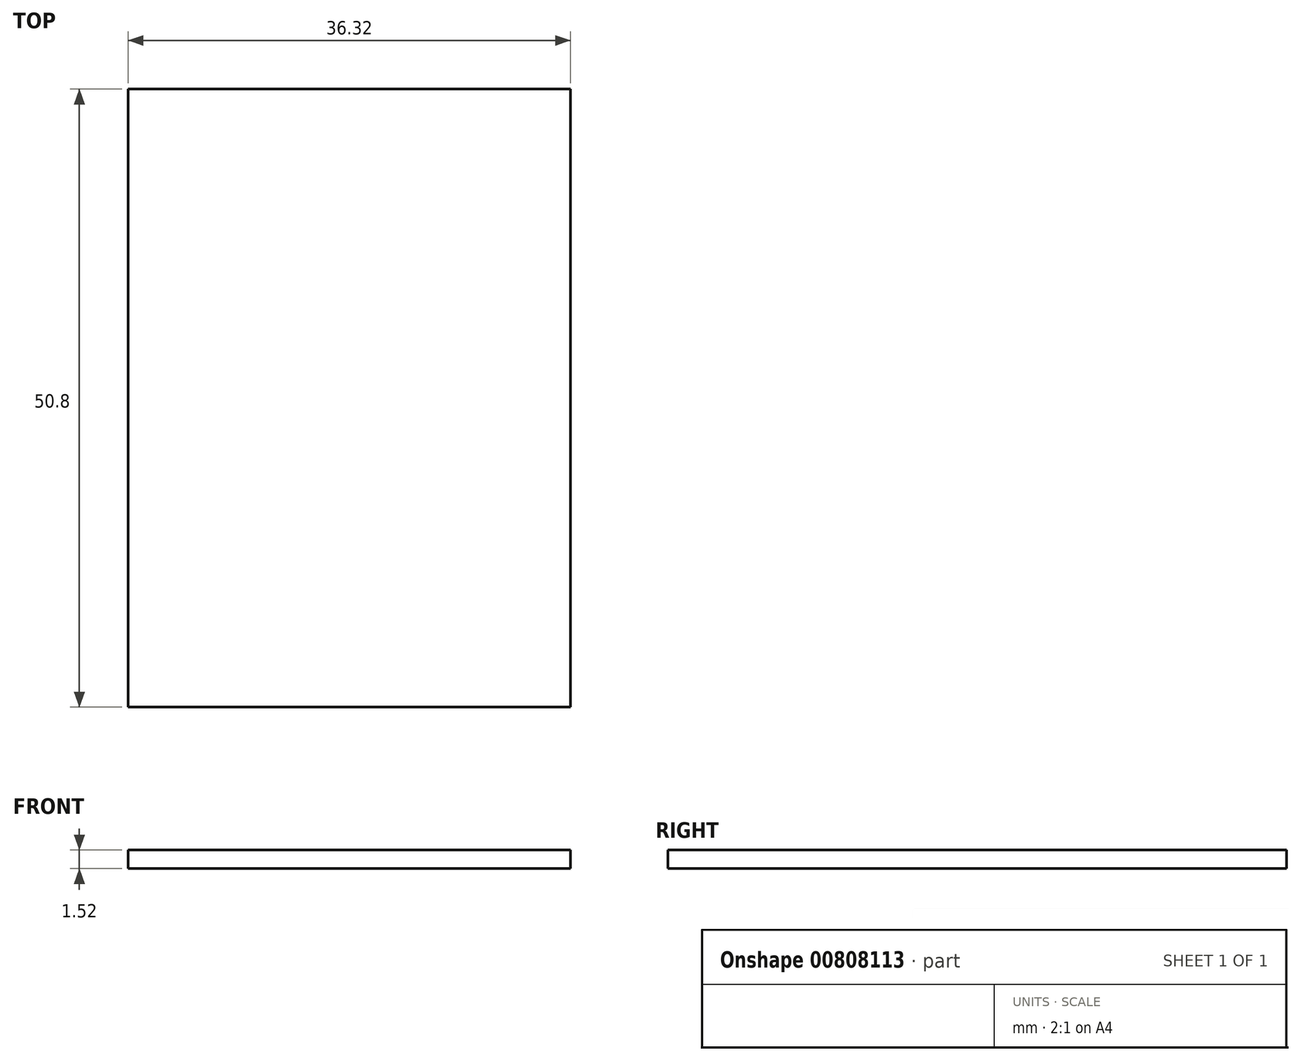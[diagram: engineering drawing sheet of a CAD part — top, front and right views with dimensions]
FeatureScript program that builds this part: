
annotation { "Feature Type Name" : "Feature", "Feature Type Description" : "" }
export const myFeature = defineFeature(function(context is Context, id is Id, definition is map)
    precondition{}
    {
        {
            var Q0;
            Q0=qCreatedBy(makeId("Top.planeOp"),FACE);
            var sketch = newSketch(context, id + "F0", { "sketchPlane" : qUnion([Q0])});
            skLineSegment(sketch, "E0.bottom", {"start": v(-58.61, 32.1) * mm, "end": v(-22.3, 32.1) * mm});
            skLineSegment(sketch, "E0.top", {"start": v(-58.61, -18.7) * mm, "end": v(-22.3, -18.7) * mm});
            skLineSegment(sketch, "E0.left", {"start": v(-58.61, 32.1) * mm, "end": v(-58.61, -18.7) * mm});
            skLineSegment(sketch, "E0.right", {"start": v(-22.3, 32.1) * mm, "end": v(-22.3, -18.7) * mm});
            skSolve(sketch);
        }
        {
            var Q0;
            Q0=qSketchRegion(id+"F0",true);
            extrude(context, id + "F1", {"entities" : qUnion([Q0]), "depth" : 1.52 * mm, "offsetDistance" : 25.4 * mm});
        }
    });
